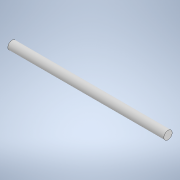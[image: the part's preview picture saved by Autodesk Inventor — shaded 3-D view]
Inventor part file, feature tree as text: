
AUTODESK INVENTOR PART (.ipt)
format: ipt  version: 2020 (Build 240168000, 168)  size: 91,648 bytes
history: native  units: mm
features: other x1, extrude x1, sketch x1
ambient origin geometry x8: Origin, YZ Plane, XZ Plane, XY Plane, X Axis, Y Axis, Z Axis, Center Point
bodies: Body1 (feature_tree)
feature tree (3):
  other  "Твердое тело1"
  extrude  "Выдавливание1"  Depth=4.0mm
  sketch  "Эскиз1"
